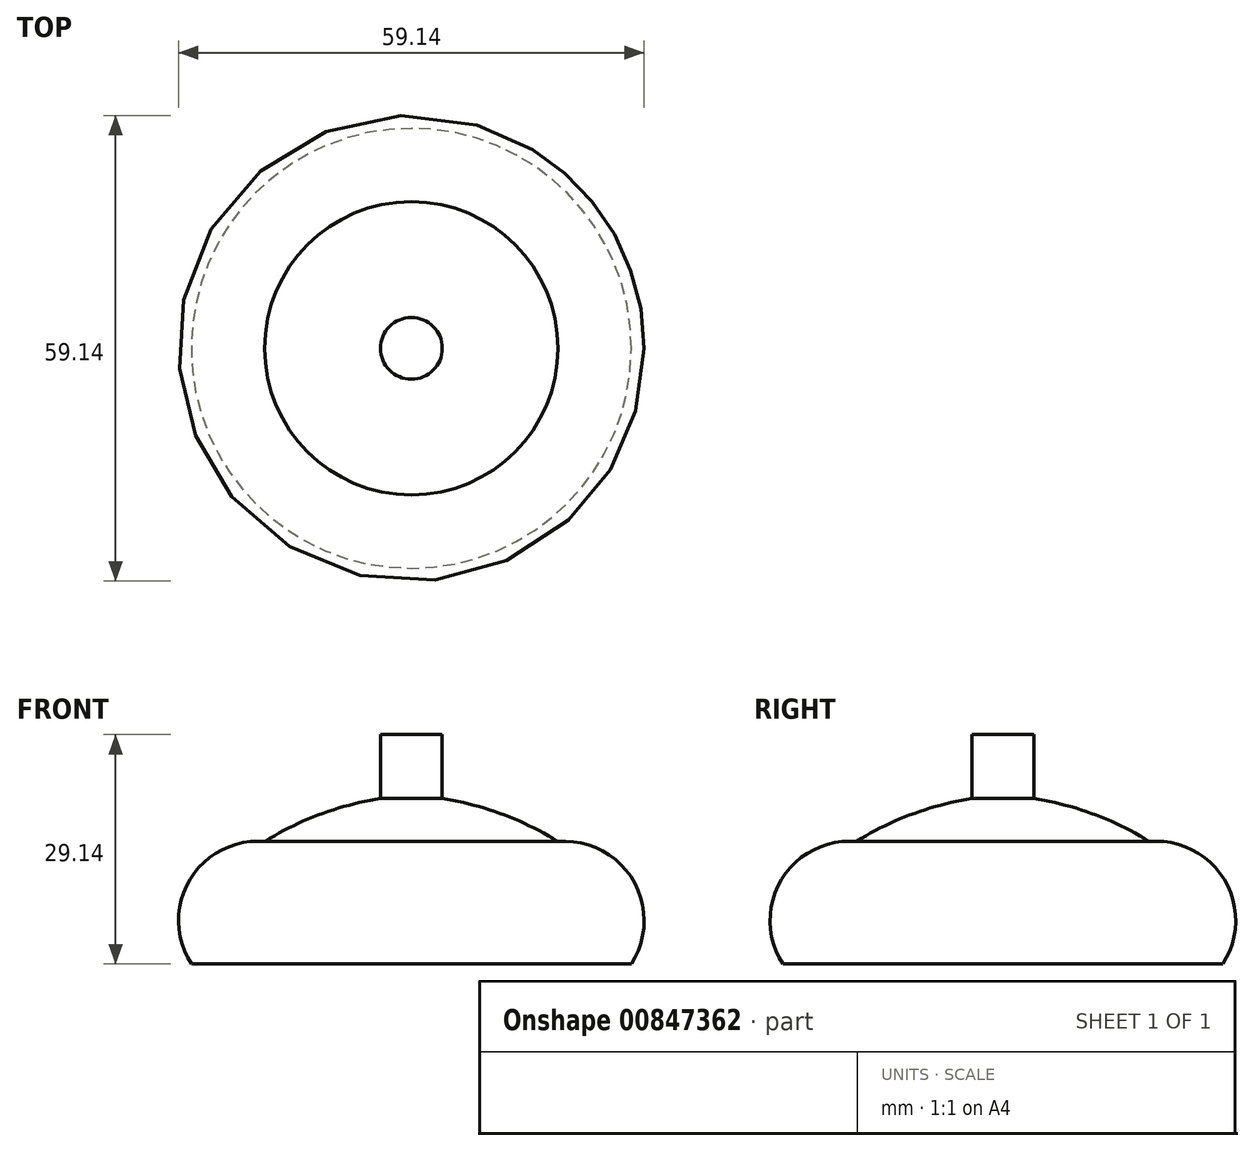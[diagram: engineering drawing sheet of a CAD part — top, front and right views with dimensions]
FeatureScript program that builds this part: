
annotation { "Feature Type Name" : "Feature", "Feature Type Description" : "" }
export const myFeature = defineFeature(function(context is Context, id is Id, definition is map)
    precondition{}
    {
        {
            var Q0;
            Q0=qCreatedBy(makeId("Front.planeOp"),FACE);
            var sketch = newSketch(context, id + "F0", { "sketchPlane" : qUnion([Q0])});
            skLineSegment(sketch, "E0", {"start": v(0, 59.5) * mm, "end": v(0, -38.52) * mm});
            skLineSegment(sketch, "E1", {"start": v(0, -38.52) * mm, "end": v(-27.94, -38.52) * mm});
            skArc(sketch, "E2", {"start": v(-18.63, -22.96) * mm, "mid": v(-28.14, -27.83) * mm, "end": v(-27.94, -38.52) * mm});
            skArc(sketch, "E3", {"start": v(-3.92, -17.51) * mm, "mid": v(-11.55, -19.5) * mm, "end": v(-18.63, -22.96) * mm});
            skLineSegment(sketch, "E4", {"start": v(-3.92, -17.51) * mm, "end": v(-3.92, -9.38) * mm});
            skLineSegment(sketch, "E5", {"start": v(-3.92, -9.38) * mm, "end": v(0, -9.38) * mm});
            skSolve(sketch);
        }
        {
            var Q0;
            Q0 = qSketchRegion(id + "F0", true);
            var Q1;
            Q1=sQuery(id+"F0.wireOp",EDGE,"E0");
            revolve(context, id + "F1", {"surfaceOperationType" : NewSurfaceOperationType.NEW, "entities" : qUnion([Q0]), "axis" : qUnion([Q1]), "revolveType" : RevolveType.FULL});
        }
    });
